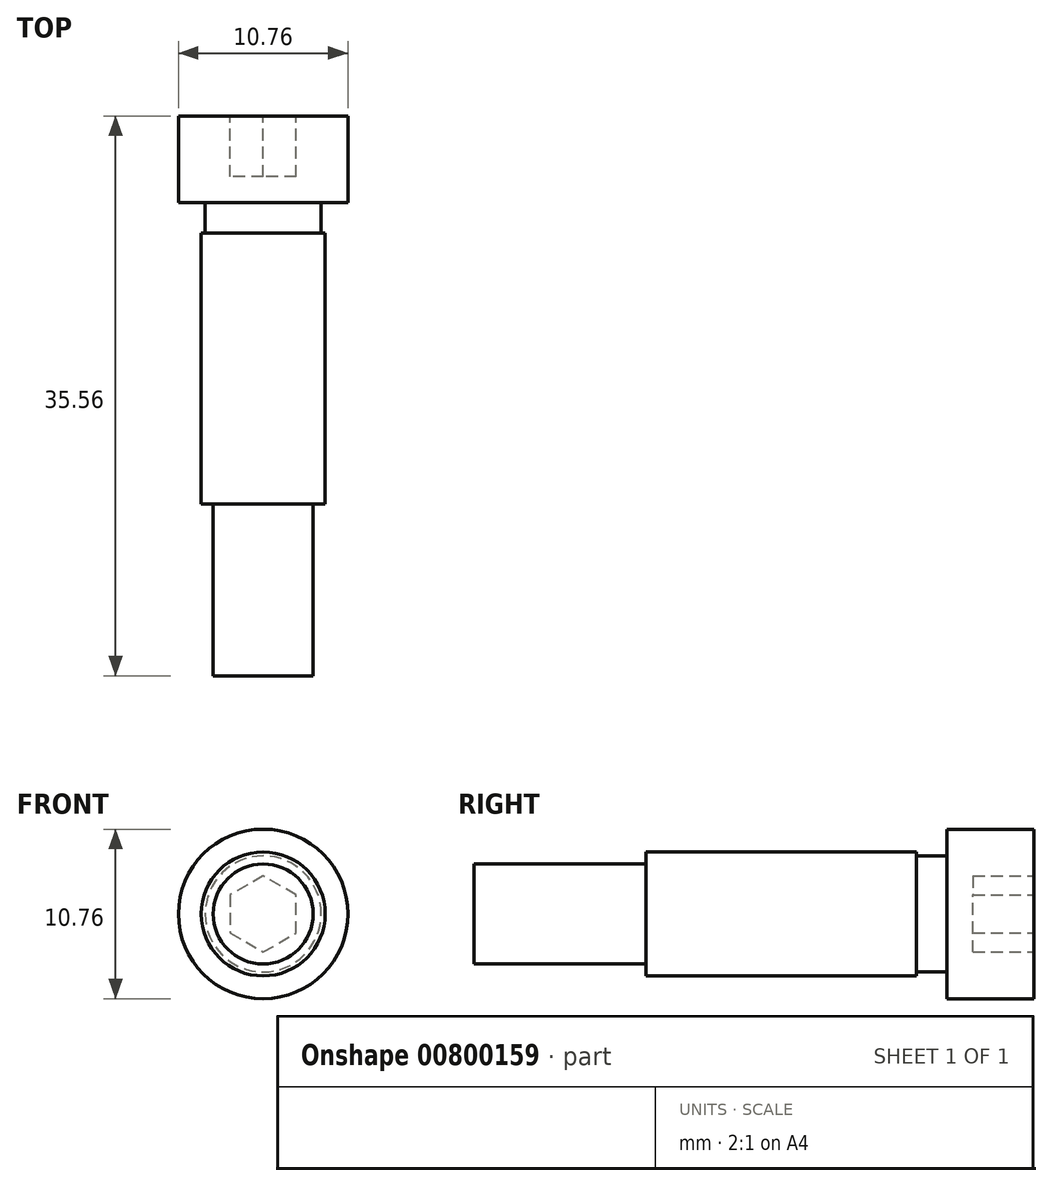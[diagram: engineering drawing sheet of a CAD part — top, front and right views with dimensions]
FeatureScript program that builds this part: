
annotation { "Feature Type Name" : "Feature", "Feature Type Description" : "" }
export const myFeature = defineFeature(function(context is Context, id is Id, definition is map)
    precondition{}
    {
        {
            var Q0;
            Q0=qCreatedBy(makeId("Right.planeOp"),FACE);
            var sketch = newSketch(context, id + "F0", { "sketchPlane" : qUnion([Q0])});
            skLineSegment(sketch, "E0", {"start": v(0, 0) * mm, "end": v(0, 3.17) * mm});
            skLineSegment(sketch, "E1", {"start": v(0, 3.18) * mm, "end": v(10.92, 3.18) * mm});
            skLineSegment(sketch, "E2", {"start": v(10.92, 3.18) * mm, "end": v(10.92, 3.94) * mm});
            skLineSegment(sketch, "E3", {"start": v(10.92, 3.94) * mm, "end": v(28.12, 3.94) * mm});
            skLineSegment(sketch, "E4", {"start": v(30.05, 3.94) * mm, "end": v(30.05, 5.38) * mm});
            skLineSegment(sketch, "E5", {"start": v(30.05, 5.38) * mm, "end": v(35.56, 5.38) * mm});
            skLineSegment(sketch, "E6", {"start": v(35.56, 5.38) * mm, "end": v(35.56, 0) * mm});
            skLineSegment(sketch, "E7", {"start": v(35.56, 0) * mm, "end": v(0, 0) * mm});
            skLineSegment(sketch, "E8", {"start": v(30.05, 3.94) * mm, "end": v(30.05, 3.68) * mm});
            skLineSegment(sketch, "E9", {"start": v(30.05, 3.68) * mm, "end": v(28.12, 3.68) * mm});
            skLineSegment(sketch, "E10", {"start": v(28.12, 3.68) * mm, "end": v(28.12, 3.94) * mm});
            skSolve(sketch);
        }
        {
            var Q0;
            Q0=qSketchRegion(id+"F0",true);
            var Q1;
            Q1=sQuery(id+"F0.wireOp",EDGE,"E7");
            revolve(context, id + "F1", {"surfaceOperationType" : NewSurfaceOperationType.NEW, "entities" : qUnion([Q0]), "axis" : qUnion([Q1]), "revolveType" : RevolveType.FULL});
        }
        {
            var Q0;
            Q0=makeQuery(id+"F1.opRevolve","SWEPT_FACE",FACE,{"disambiguationData":[OSD([sQuery(id+"F0.wireOp",EDGE,"E6")])]});
            var sketch = newSketch(context, id + "F2", { "sketchPlane" : qUnion([Q0])});
            skCircle(sketch, "E11.cCircle", {"center": v(0, 0) * mm, "radius": 2.1 * mm, "construction": true});
            skLineSegment(sketch, "E11.0", {"start": v(0, 2.42) * mm, "end": v(2.1, 1.2) * mm});
            skLineSegment(sketch, "E11.1", {"start": v(2.1, 1.2) * mm, "end": v(2.1, -1.2) * mm});
            skLineSegment(sketch, "E11.2", {"start": v(2.1, -1.2) * mm, "end": v(0, -2.42) * mm});
            skLineSegment(sketch, "E11.3", {"start": v(0, -2.42) * mm, "end": v(-2.1, -1.2) * mm});
            skLineSegment(sketch, "E11.4", {"start": v(-2.1, -1.2) * mm, "end": v(-2.1, 1.2) * mm});
            skLineSegment(sketch, "E11.5", {"start": v(-2.1, 1.2) * mm, "end": v(0, 2.42) * mm});
            skPoint(sketch, "E11.0.midPoint", {"position": v(1.05, 1.81) * mm});
            skSolve(sketch);
        }
        {
            var Q0;
            Q0=qSketchRegion(id+"F2",true);
            extrude(context, id + "F3", {"entities" : qUnion([Q0]), "operationType" : NewBodyOperationType.REMOVE, "oppositeDirection" : true, "depth" : 3.86 * mm, "offsetDistance" : 25.4 * mm});
        }
    });
